# Revit family: Bathtub_Commercial_FBY1700P_TOTO
name_source: partatom
category: Plumbing Fixtures
revit_build: Autodesk Revit Architecture 2013 (Build: 20130531_2115(x64)
units: mm (PartAtom-declared; Revit-internal decimal feet)

## types (1)
- FBY1700P
    04 CSI = 22 42 19
    95 CSI = 15410
    ADA Compliant = Yes
    Assembly Code = D2010510
    CAD Drawing URL = http://assets.totousa.com
    Color Availability = #01  Cotton, #12  Sedona Beige
    Default Elevation = 48"
    Depth = 66"
    Description = Enameled Cast Iron Bathtub
    Finish = Metal - TOTO - Chrome - Polished
    Height = 18 5/16"
    Manufacturer = TOTO USA, Inc.
    Manufacturer Fax = (770) 282-0002
    Model = FBY1700P
    Shipping Weight = 309.00 lb
    Spec Sheet URL = http://assets.totousa.com
    Style = Commercial
    Subcategory = Bathtubs
    Toto BIM Number = BM-00066
    URL = http://www.totousa.com
    Warranty = Lifetime Limited Warranty
    Warranty URL = http://www.totousa.com
    Waste Connection NPT = 2 1/4"
    Waste Connection Radius = 1 1/8"
    Width = 32"

## geometry (parser evidence)
native form markers: Blend x24, Sweep x2
no freeform markers — native parametric forms only
